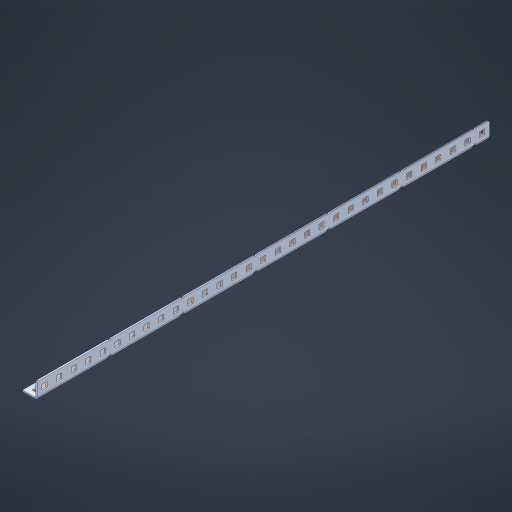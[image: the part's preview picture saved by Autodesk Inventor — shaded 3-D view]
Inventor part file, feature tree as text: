
AUTODESK INVENTOR PART (.ipt)
format: ipt  version: 2023 (Build 270158000, 158)  size: 971,264 bytes
history: native  units: in
note: dims shown in document units (in); Inventor stores cm internally (conversion verified against a paired STEP export)
features: other x67, extrude x61, sheet_metal_op x10, sketch x8, mirror x1, pattern_linear x1, chamfer x1
ambient origin geometry x8: Origin, YZ Plane, XZ Plane, XY Plane, X Axis, Y Axis, Z Axis, Center Point
bodies: Solid1 (feature_tree), Body (feature_tree)
feature tree (149):
  other  "Flange Pattern Plane"
  sheet_metal_op  "Flange Pattern"
  sheet_metal_op  "Body Pattern"
  other  "Arc Length"
  mirror  "Notch Mirror"
  pattern_linear  "Notch Pattern"  Spacing1=0.1875in  [1 undecoded]
  chamfer  "End Chamfer"
  extrude  "Half Cut"  Depth=0.0469in
  sketch  "Sketch1"  dims[d0=2.5in]
  other  "Plate1"
  sketch  "Sketch2"  dims[d1=15.5in]
  other  "Plate2"
  sheet_metal_op  "Bend1"
  sheet_metal_op  "Corner1"
  sketch  "Sketch3"  dims[d2=0.0469in]
  other  "Flange Pattern Sketch"
  sketch  "Sketch7"  dims[d3=0.0469in]
  other  "Srf1"
  other  "Srf2"
  sketch  "Sketch8"  dims[d4=0.0234in]
  sketch  "Sketch9"  dims[d5=0.0938in]
  other  "Srf91"
  sheet_metal_op  "Body Pattern Sketch"
  other  "Srf92"
  sketch  "Sketch13"  dims[d6=0.0469in]
  sketch  "Sketch14"  dims[d7=0.5in d8=90.0deg d9=0.0312in d10=0.1875in d11=0.0469in d12=0.0469in d16=0.182in d17=0.02in d18=0.0469in d19=0.0in d20=0.25in d21=0.25in d46=0.172in d47=1.0in d48=0.0in d49=0.182in d50=0.02in d51=0.25in d52=0.25in d53=0.0469in d54=0.0in d55=0.172in d56=1.0in d57=0.0in d60=12.2047in d62=0.5in d63=0.3937in d65=0.5in d85=0.1227in d86=0.1659in d88=0.04in d89=0.0469in d90=0.0in d91=0.04in d92=0.0491in d95=2.5in d96=0.04in d97=0.25in d98=45.0deg d101=0.0in d102=2.497in d131=0.5in d132=12.2047in d134=0.5in d139=0.5in]
  other  "Srf856"
  other  "Srf1310"
  other  "Srf1311"
  other  "Srf1312"
  other  "Srf1376"
  other  "Srf1377"
  other  "Srf1728"
  other  "Srf1755"
  other  "Srf1878"
  other  "Srf1879"
  other  "Srf1880"
  other  "Srf1881"
  other  "Srf1882"
  other  "Srf1883"
  other  "Srf1884"
  other  "Srf1885"
  other  "Srf1886"
  other  "Srf1887"
  other  "Srf1888"
  other  "Srf1889"
  other  "Srf1890"
  other  "Srf1891"
  other  "Srf1892"
  other  "Srf1893"
  other  "Srf1894"
  other  "Srf1895"
  other  "Srf1896"
  other  "Srf1897"
  other  "Srf1898"
  other  "Srf1899"
  other  "Srf1900"
  other  "Srf1901"
  other  "Srf1902"
  other  "Srf1942"
  other  "Srf1943"
  other  "Srf1944"
  other  "Srf1945"
  other  "Srf1946"
  other  "Srf1947"
  other  "Srf1948"
  other  "Srf1949"
  other  "Srf1950"
  other  "Srf1951"
  other  "Srf1952"
  other  "Srf1953"
  other  "Srf1954"
  other  "Srf1955"
  other  "Srf1956"
  other  "Srf1957"
  other  "Srf1958"
  other  "Srf1959"
  other  "Srf1960"
  other  "Srf1961"
  other  "Srf1962"
  other  "Srf1963"
  other  "Srf1964"
  other  "Srf1965"
  other  "Srf1966"
  sheet_metal_op  "Flange Stamp"
  sheet_metal_op  "Flange Circle"
  sheet_metal_op  "Body Stamp"
  sheet_metal_op  "Body Circle"
  sheet_metal_op  "Notch"
  extrude  "ExtrusionSrf2"  Depth=0.0469in
  extrude  "ExtrusionSrf92"  Depth=0.5in
  extrude  "ExtrusionSrf856"  Depth=0.02in
  extrude  "ExtrusionSrf1310"  Depth=0.0469in
  extrude  "ExtrusionSrf1311"  TaperAngle=0.0deg  [1 undecoded]
  extrude  "ExtrusionSrf1312"  Depth=0.5in
  extrude  "ExtrusionSrf1376"  Depth=0.5in
  extrude  "ExtrusionSrf1377"  Depth=0.5in
  extrude  "ExtrusionSrf1728"  Depth=0.5in TaperAngle=0.0deg
  extrude  "ExtrusionSrf1755"  Depth=0.5in
  extrude  "ExtrusionSrf1878"  Depth=0.02in
  extrude  "ExtrusionSrf1879"  Depth=0.5in
  extrude  "ExtrusionSrf1880"  Depth=0.5in
  extrude  "ExtrusionSrf1881"  Depth=0.0469in
  extrude  "ExtrusionSrf1882"  TaperAngle=0.0deg  [1 undecoded]
  extrude  "ExtrusionSrf1883"  Depth=0.5in
  extrude  "ExtrusionSrf1884"  Depth=0.5in TaperAngle=0.0deg
  extrude  "ExtrusionSrf1885"  Depth=0.5in
  extrude  "ExtrusionSrf1886"  Depth=0.5in
  extrude  "ExtrusionSrf1887"  Depth=0.5in
  extrude  "ExtrusionSrf1888"  Depth=0.5in
  extrude  "ExtrusionSrf1889"  Depth=0.5in
  extrude  "ExtrusionSrf1890"  Depth=0.0469in
  extrude  "ExtrusionSrf1891"  TaperAngle=0.0deg  [1 undecoded]
  extrude  "ExtrusionSrf1892"  Depth=0.5in
  extrude  "ExtrusionSrf1893"  Depth=0.5in
  extrude  "ExtrusionSrf1894"  Depth=0.5in
  extrude  "ExtrusionSrf1895"  Depth=0.5in TaperAngle=45.0deg
  extrude  "ExtrusionSrf1896"  TaperAngle=0.0deg  [1 undecoded]
  extrude  "ExtrusionSrf1897"  Depth=0.5in
  extrude  "ExtrusionSrf1898"  Depth=0.5in
  extrude  "ExtrusionSrf1899"  Depth=0.5in
  extrude  "ExtrusionSrf1900"  Depth=0.5in
  extrude  "ExtrusionSrf1901"  Depth=0.5in
  extrude  "ExtrusionSrf1902"  [1 undecoded]
  extrude  "ExtrusionSrf1942"  [1 undecoded]
  extrude  "ExtrusionSrf1943"  [1 undecoded]
  extrude  "ExtrusionSrf1944"  [1 undecoded]
  extrude  "ExtrusionSrf1945"  [1 undecoded]
  extrude  "ExtrusionSrf1946"  [1 undecoded]
  extrude  "ExtrusionSrf1947"  [1 undecoded]
  extrude  "ExtrusionSrf1948"  [1 undecoded]
  extrude  "ExtrusionSrf1949"  [1 undecoded]
  extrude  "ExtrusionSrf1950"  [1 undecoded]
  extrude  "ExtrusionSrf1951"  [1 undecoded]
  extrude  "ExtrusionSrf1952"  [1 undecoded]
  extrude  "ExtrusionSrf1953"  [1 undecoded]
  extrude  "ExtrusionSrf1954"  [1 undecoded]
  extrude  "ExtrusionSrf1955"  [1 undecoded]
  extrude  "ExtrusionSrf1956"  [1 undecoded]
  extrude  "ExtrusionSrf1957"  [1 undecoded]
  extrude  "ExtrusionSrf1958"  [1 undecoded]
  extrude  "ExtrusionSrf1959"  [1 undecoded]
  extrude  "ExtrusionSrf1960"  [1 undecoded]
  extrude  "ExtrusionSrf1961"  [1 undecoded]
  extrude  "ExtrusionSrf1962"  [1 undecoded]
  extrude  "ExtrusionSrf1963"  [1 undecoded]
  extrude  "ExtrusionSrf1964"  [1 undecoded]
  extrude  "ExtrusionSrf1965"  [1 undecoded]
  extrude  "ExtrusionSrf1966"  [1 undecoded]
note: 31 required parameter values undecoded (feature->parameter linkage not recoverable at this tier; creation-order binding heuristic only, values carry confidence <= 0.55)
